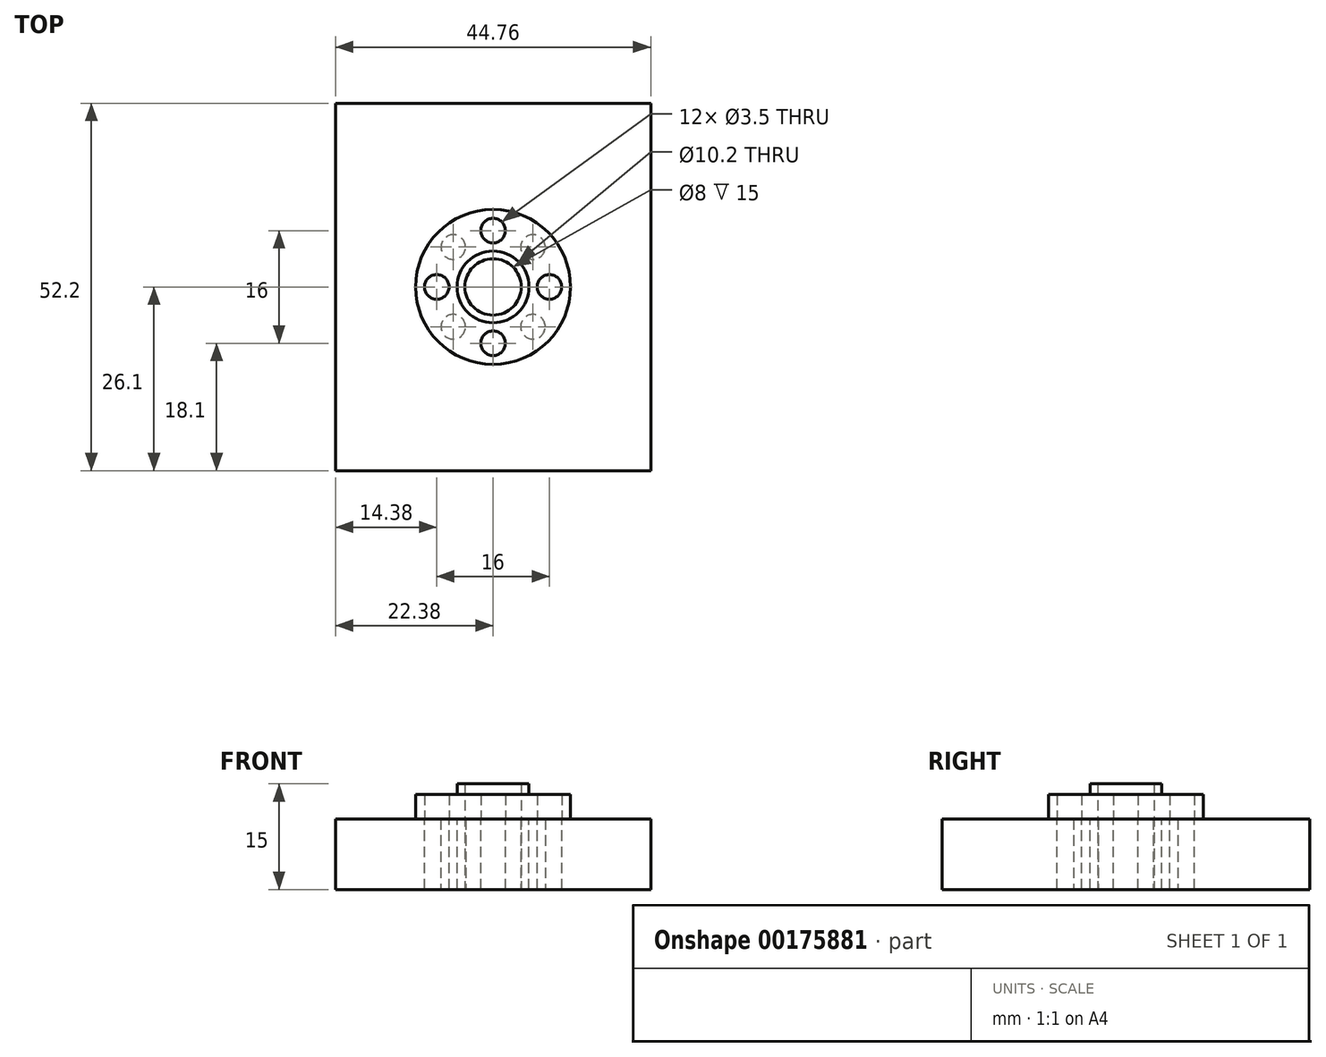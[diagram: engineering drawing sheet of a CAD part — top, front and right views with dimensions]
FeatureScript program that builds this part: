
annotation { "Feature Type Name" : "Feature", "Feature Type Description" : "" }
export const myFeature = defineFeature(function(context is Context, id is Id, definition is map)
    precondition{}
    {
        {
            var Q0;
            Q0=qCreatedBy(makeId("Top.planeOp"),FACE);
            var sketch = newSketch(context, id + "F0", { "sketchPlane" : qUnion([Q0])});
            skCircle(sketch, "E0", {"center": v(0, 0) * mm, "radius": 11 * mm});
            skCircle(sketch, "E1", {"center": v(-8, 0) * mm, "radius": 1.75 * mm});
            skCircle(sketch, "E2", {"center": v(0, 0) * mm, "radius": 8 * mm, "construction": true});
            skCircle(sketch, "E3", {"center": v(0, 8) * mm, "radius": 1.75 * mm});
            skCircle(sketch, "E4", {"center": v(8, 0) * mm, "radius": 1.75 * mm});
            skCircle(sketch, "E5", {"center": v(0, -8) * mm, "radius": 1.75 * mm});
            skCircle(sketch, "E6", {"center": v(0, 0) * mm, "radius": 4 * mm});
            skSolve(sketch);
        }
        {
            var Q0;
            Q0 = qSketchRegion(id + "F0", true);
            extrude(context, id + "F1", {"entities" : qUnion([Q0]), "depth" : 3.5 * mm});
        }
        {
            var Q0;
            Q0=makeQuery(id+"F1.opExtrude","CAP_FACE",FACE,{"disambiguationData":[OSD([sQuery(id+"F0.wireOp",EDGE,"E0"),sQuery(id+"F0.wireOp",EDGE,"E1"),sQuery(id+"F0.wireOp",EDGE,"E3"),sQuery(id+"F0.wireOp",EDGE,"E4"),sQuery(id+"F0.wireOp",EDGE,"E5"),sQuery(id+"F0.wireOp",EDGE,"E6")])],"isStart":false});
            var sketch = newSketch(context, id + "F2", { "sketchPlane" : qUnion([Q0])});
            skCircle(sketch, "E7", {"center": v(0, 0) * mm, "radius": 5.1 * mm});
            skCircle(sketch, "E8.0", {"center": v(0, 0) * mm, "radius": 4 * mm});
            skSolve(sketch);
        }
        {
            var Q0;
            Q0 = qSketchRegion(id + "F2", true);
            extrude(context, id + "F3", {"entities" : qUnion([Q0]), "operationType" : NewBodyOperationType.ADD, "depth" : 1.5 * mm});
        }
        {
            var Q0;
            Q0=makeQuery(id+"F1.opExtrude","CAP_FACE",FACE,{"disambiguationData":[OSD([sQuery(id+"F0.wireOp",EDGE,"E0"),sQuery(id+"F0.wireOp",EDGE,"E1"),sQuery(id+"F0.wireOp",EDGE,"E3"),sQuery(id+"F0.wireOp",EDGE,"E4"),sQuery(id+"F0.wireOp",EDGE,"E5"),sQuery(id+"F0.wireOp",EDGE,"E6")])],"isStart":true});
            var sketch = newSketch(context, id + "F4", { "sketchPlane" : qUnion([Q0])});
            skCircle(sketch, "E9.0", {"center": v(0, 0) * mm, "radius": 4 * mm});
            skCircle(sketch, "E10.0", {"center": v(0, 0) * mm, "radius": 5.1 * mm});
            skSolve(sketch);
        }
        {
            var Q0;
            Q0 = qSketchRegion(id + "F4", true);
            extrude(context, id + "F5", {"entities" : qUnion([Q0]), "operationType" : NewBodyOperationType.ADD, "depth" : 10 * mm});
        }
        {
            var Q0;
            Q0=makeQuery(id+"F1.opExtrude","CAP_FACE",FACE,{"disambiguationData":[OSD([sQuery(id+"F0.wireOp",EDGE,"E0"),sQuery(id+"F0.wireOp",EDGE,"E1"),sQuery(id+"F0.wireOp",EDGE,"E3"),sQuery(id+"F0.wireOp",EDGE,"E4"),sQuery(id+"F0.wireOp",EDGE,"E5"),sQuery(id+"F0.wireOp",EDGE,"E6")])],"isStart":true});
            var sketch = newSketch(context, id + "F6", { "sketchPlane" : qUnion([Q0])});
            skLineSegment(sketch, "E11.bottom", {"start": v(-22.38, 26.1) * mm, "end": v(22.38, 26.1) * mm});
            skLineSegment(sketch, "E11.top", {"start": v(-22.38, -26.1) * mm, "end": v(22.38, -26.1) * mm});
            skLineSegment(sketch, "E11.left", {"start": v(-22.38, 26.1) * mm, "end": v(-22.38, -26.1) * mm});
            skLineSegment(sketch, "E11.right", {"start": v(22.38, 26.1) * mm, "end": v(22.38, -26.1) * mm});
            skPoint(sketch, "E11.middle", {"position": v(0, 0) * mm});
            skCircle(sketch, "E12.0", {"center": v(0, 0) * mm, "radius": 5.1 * mm});
            skCircle(sketch, "E13.0", {"center": v(0, 8) * mm, "radius": 1.75 * mm});
            skCircle(sketch, "E14.0", {"center": v(-8, 0) * mm, "radius": 1.75 * mm});
            skCircle(sketch, "E15.0", {"center": v(0, -8) * mm, "radius": 1.75 * mm});
            skCircle(sketch, "E16.0", {"center": v(8, 0) * mm, "radius": 1.75 * mm});
            skSolve(sketch);
        }
        {
            var Q0;
            Q0 = qSketchRegion(id + "F6", true);
            extrude(context, id + "F7", {"entities" : qUnion([Q0]), "depth" : 10 * mm});
        }
        {
            var Q0;
            Q0=makeQuery(id+"F7.opExtrude","CAP_FACE",FACE,{"disambiguationData":[OSD([sQuery(id+"F6.wireOp",EDGE,"E11.bottom"),sQuery(id+"F6.wireOp",EDGE,"E11.top"),sQuery(id+"F6.wireOp",EDGE,"E11.left"),sQuery(id+"F6.wireOp",EDGE,"E11.right"),sQuery(id+"F6.wireOp",EDGE,"E12.0"),sQuery(id+"F6.wireOp",EDGE,"E13.0"),sQuery(id+"F6.wireOp",EDGE,"E14.0"),sQuery(id+"F6.wireOp",EDGE,"E15.0"),sQuery(id+"F6.wireOp",EDGE,"E16.0")])],"isStart":false});
            var sketch = newSketch(context, id + "F8", { "sketchPlane" : qUnion([Q0])});
            skPoint(sketch, "E17", {"position": v(0, 8) * mm});
            skCircle(sketch, "E18", {"center": v(0, 0) * mm, "radius": 8 * mm, "construction": true});
            skCircle(sketch, "E19", {"center": v(-5.66, 5.66) * mm, "radius": 1.75 * mm});
            skCircle(sketch, "E20", {"center": v(5.66, 5.66) * mm, "radius": 1.75 * mm});
            skCircle(sketch, "E21", {"center": v(5.66, -5.66) * mm, "radius": 1.75 * mm});
            skCircle(sketch, "E22", {"center": v(-5.66, -5.66) * mm, "radius": 1.75 * mm});
            skLineSegment(sketch, "E23", {"start": v(-5.66, 5.66) * mm, "end": v(5.66, -5.66) * mm, "construction": true});
            skLineSegment(sketch, "E24", {"start": v(5.66, 5.66) * mm, "end": v(-5.66, -5.66) * mm, "construction": true});
            skSolve(sketch);
        }
        {
            var Q0;
            Q0 = qSketchRegion(id + "F8", true);
            extrude(context, id + "F9", {"entities" : qUnion([Q0]), "operationType" : NewBodyOperationType.REMOVE, "oppositeDirection" : true, "depth" : 10 * mm});
        }
    });
